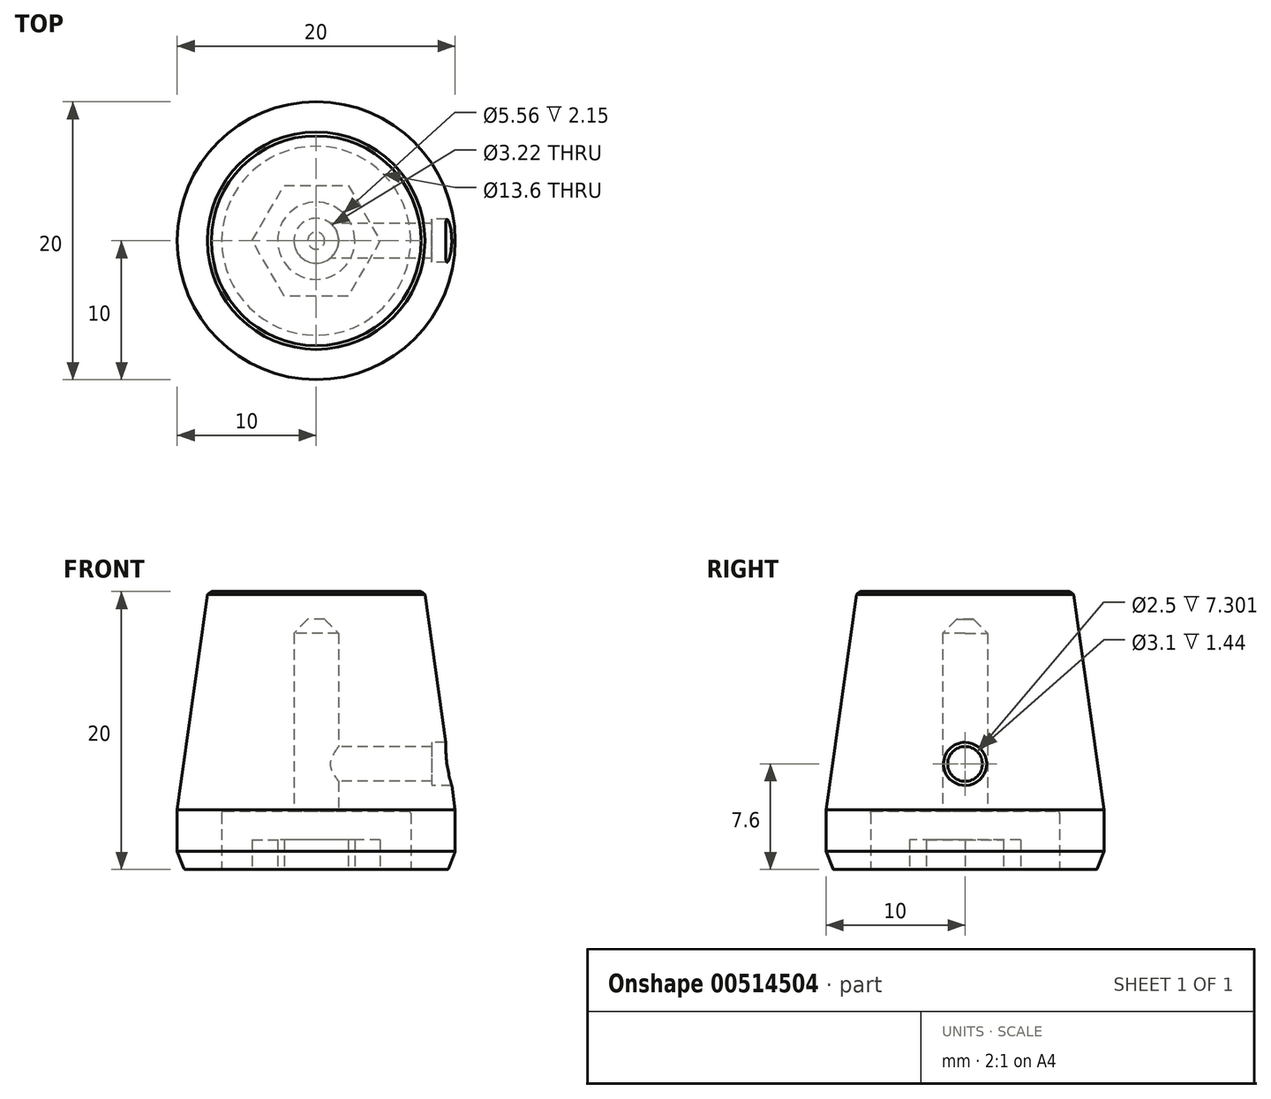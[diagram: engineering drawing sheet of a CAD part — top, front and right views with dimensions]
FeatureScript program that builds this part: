
annotation { "Feature Type Name" : "Feature", "Feature Type Description" : "" }
export const myFeature = defineFeature(function(context is Context, id is Id, definition is map)
    precondition{}
    {
        {
            assignVariable(context, id + "F0", {"name" : "majorOD", "anyValue" : 20});
        }
        {
            var Q0;
            Q0=qCreatedBy(makeId("Front.planeOp"),FACE);
            var sketch = newSketch(context, id + "F1", { "sketchPlane" : qUnion([Q0])});
            skLineSegment(sketch, "E0.bottom", {"start": v(6.8, 0) * mm, "end": v(9.5, 0) * mm});
            skLineSegment(sketch, "E0.top", {"start": v(0, 20) * mm, "end": v(7.8, 20) * mm});
            skLineSegment(sketch, "E0.left", {"start": v(0, 4.2) * mm, "end": v(0, 20) * mm, "construction": true});
            skLineSegment(sketch, "E0.right", {"start": v(10, 1.3) * mm, "end": v(10, 4.3) * mm});
            skLineSegment(sketch, "E1", {"start": v(1.6, 4.2) * mm, "end": v(6.8, 4.2) * mm});
            skLineSegment(sketch, "E2", {"start": v(6.8, 4.2) * mm, "end": v(6.8, 0) * mm});
            skLineSegment(sketch, "E3", {"start": v(1.6, 4.2) * mm, "end": v(1.6, 18) * mm});
            skLineSegment(sketch, "E4", {"start": v(1.6, 18) * mm, "end": v(0, 18) * mm});
            skLineSegment(sketch, "E5", {"start": v(0, 20) * mm, "end": v(0, 18) * mm});
            skPoint(sketch, "E6", {"position": v(0, 7.6) * mm});
            skLineSegment(sketch, "E7", {"start": v(7.8, 20) * mm, "end": v(10, 4.3) * mm});
            skLineSegment(sketch, "E8", {"start": v(10, 4.3) * mm, "end": v(10, 20.36) * mm, "construction": true});
            skPoint(sketch, "E9", {"position": v(0, 0) * mm});
            skLineSegment(sketch, "E10", {"start": v(0, 7.6) * mm, "end": v(10, 7.6) * mm, "construction": true});
            skPoint(sketch, "E11", {"position": v(10, 7.6) * mm});
            skLineSegment(sketch, "E12", {"start": v(10, 1.3) * mm, "end": v(9.5, 0) * mm});
            skSolve(sketch);
        }
        {
            var Q0;
            Q0=qSketchRegion(id+"F1",true);
            var Q1;
            Q1=sQuery(id+"F1.wireOp",EDGE,"E0.left");
            revolve(context, id + "F2", {"entities" : qUnion([Q0]), "axis" : qUnion([Q1]), "revolveType" : RevolveType.FULL});
        }
        {
            var Q0;
            Q0=makeQuery(id+"F2.opRevolve","SWEPT_EDGE",EDGE,{"disambiguationData":[OSD([sQuery(id+"F1.wireOp",EDGE,"E3"),sQuery(id+"F1.wireOp",EDGE,"E4")])]});
            chamfer(context, id + "F3", {"entities" : qUnion([Q0]), "width" : 1 * mm, "tangentPropagation" : true});
        }
        {
            var Q0;
            Q0=makeQuery(id+"F2.opRevolve","SWEPT_EDGE",EDGE,{"disambiguationData":[OSD([sQuery(id+"F1.wireOp",EDGE,"E0.top"),sQuery(id+"F1.wireOp",EDGE,"E7")])]});
            chamfer(context, id + "F4", {"entities" : qUnion([Q0]), "chamferType" : ChamferType.TWO_OFFSETS, "width1" : .25 * mm, "oppositeDirection" : false, "width2" : .2 * mm, "tangentPropagation" : true});
        }
        {
            var Q0;
            Q0=makeQuery(id+"F2.opRevolve","SWEPT_FACE",FACE,{"disambiguationData":[OSD([sQuery(id+"F1.wireOp",EDGE,"E0.bottom")])]});
            var Q1;
            Q1=makeQuery(id+"F2.opRevolve","SWEPT_EDGE",EDGE,{"disambiguationData":[OSD([sQuery(id+"F1.wireOp",EDGE,"E1"),sQuery(id+"F1.wireOp",EDGE,"E2")])]});
            var Q2;
            Q2=makeQuery(id+"F2.opRevolve","SWEPT_EDGE",EDGE,{"disambiguationData":[OSD([sQuery(id+"F1.wireOp",EDGE,"E1"),sQuery(id+"F1.wireOp",EDGE,"E3")])]});
            var Q3;
            Q3=makeQuery(id+"FZYC6JOD7CXebZJ_1.opChamfer","BLEND_EDGE",EDGE,{"blendedFrom":[makeQuery(id+"F2.opRevolve","SWEPT_EDGE",EDGE,{"disambiguationData":[OSD([sQuery(id+"F1.wireOp",EDGE,"E0.right"),sQuery(id+"F1.wireOp",EDGE,"vCOGe3Q2-wI1u-JRl4-NgCf-ssfP025QzTOs")])]}),makeQuery(id+"F2.opRevolve","SWEPT_FACE",FACE,{"disambiguationData":[OSD([sQuery(id+"F1.wireOp",EDGE,"BSaUtDve-KYLm-bPJ0-ROIl-rT6jKh3f8Nbx")])]})],"blendedInto":[makeQuery(id+"F2.opRevolve","SWEPT_FACE",FACE,{"disambiguationData":[OSD([sQuery(id+"F1.wireOp",EDGE,"BSaUtDve-KYLm-bPJ0-ROIl-rT6jKh3f8Nbx")])]})]});
            fillet(context, id + "F5", {"entities" : qUnion([Q0, Q1, Q2, Q3]), "radius" : 0.15 * mm, "tangentPropagation" : true, "allowEdgeOverflow" : false});
        }
        {
            var Q0;
            Q0=sQuery(id+"F1.wireOp",EDGE,"E0.right");
            cPlane(context, id + "F6", {"entities" : qUnion([Q0]), "cplaneType" : CPlaneType.LINE_ANGLE, "offset" : 25 * mm, "angle" : 0 * degree, "width" : 150 * mm, "height" : 150 * mm});
        }
        {
            var Q0;
            Q0=qCreatedBy(id+"F6.planeOp",FACE);
            var sketch = newSketch(context, id + "F7", { "sketchPlane" : qUnion([Q0])});
            skPoint(sketch, "E13.0", {"position": v(0, 7.6) * mm});
            skSolve(sketch);
        }
        {
            var Q0;
            Q0=sQuery(id+"F7.wireOp",VERTEX,"E13.0");
            var Q1;
            Q1=makeQuery(id+"F2.opRevolve","SWEPT_BODY",BODY,{"disambiguationData":[OSD([sQuery(id+"F1.wireOp",EDGE,"E0.bottom"),sQuery(id+"F1.wireOp",EDGE,"E0.top"),sQuery(id+"F1.wireOp",EDGE,"E0.right"),sQuery(id+"F1.wireOp",EDGE,"E1"),sQuery(id+"F1.wireOp",EDGE,"E2"),sQuery(id+"F1.wireOp",EDGE,"BSaUtDve-KYLm-bPJ0-ROIl-rT6jKh3f8Nbx"),sQuery(id+"F1.wireOp",EDGE,"vCOGe3Q2-wI1u-JRl4-NgCf-ssfP025QzTOs"),sQuery(id+"F1.wireOp",EDGE,"E3"),sQuery(id+"F1.wireOp",EDGE,"E4"),sQuery(id+"F1.wireOp",EDGE,"E5"),sQuery(id+"F1.wireOp",EDGE,"E7")])]});
            hole(context, id + "F8", {"style" : HoleStyle.C_BORE, "endStyle" : HoleEndStyle.BLIND, "holeDiameter" : 2.5 * mm, "cBoreDiameter" : 3.1 * mm, "cBoreDepth" : 1 * mm, "majorDiameter" : 5 * mm, "holeDepth" : (getVariable(context, 'majorOD') / 2) * mm, "isTappedThrough" : true, "tappedDepth" : 12 * mm, "tapClearance" : 3, "locations" : qUnion([Q0]), "scope" : qUnion([Q1]), "startStyle" : HoleStartStyle.PART});
        }
        {
            var Q0;
            Q0=qCreatedBy(makeId("Top.planeOp"),FACE);
            var sketch = newSketch(context, id + "F9", { "sketchPlane" : qUnion([Q0])});
            skCircle(sketch, "E14.cCircle", {"center": v(0, 0) * mm, "radius": 4 * mm, "construction": true});
            skLineSegment(sketch, "E14.0", {"start": v(2.3, -4) * mm, "end": v(-2.3, -4) * mm});
            skLineSegment(sketch, "E14.1", {"start": v(-2.3, -4) * mm, "end": v(-4.6, 0) * mm});
            skLineSegment(sketch, "E14.2", {"start": v(-4.6, 0) * mm, "end": v(-2.3, 4) * mm});
            skLineSegment(sketch, "E14.3", {"start": v(-2.3, 4) * mm, "end": v(2.3, 4) * mm});
            skLineSegment(sketch, "E14.4", {"start": v(2.3, 4) * mm, "end": v(4.6, 0) * mm});
            skLineSegment(sketch, "E14.5", {"start": v(4.6, 0) * mm, "end": v(2.3, -4) * mm});
            skPoint(sketch, "E14.0.midPoint", {"position": v(0, -4) * mm});
            skCircle(sketch, "E15", {"center": v(0, 0) * mm, "radius": 2.78 * mm});
            skSolve(sketch);
        }
        {
            var Q0;
            Q0=qSketchRegion(id+"F9",true);
            extrude(context, id + "F10", {"entities" : qUnion([Q0]), "depth" : 2.15 * mm, "offsetDistance" : 25 * mm});
        }
    });
